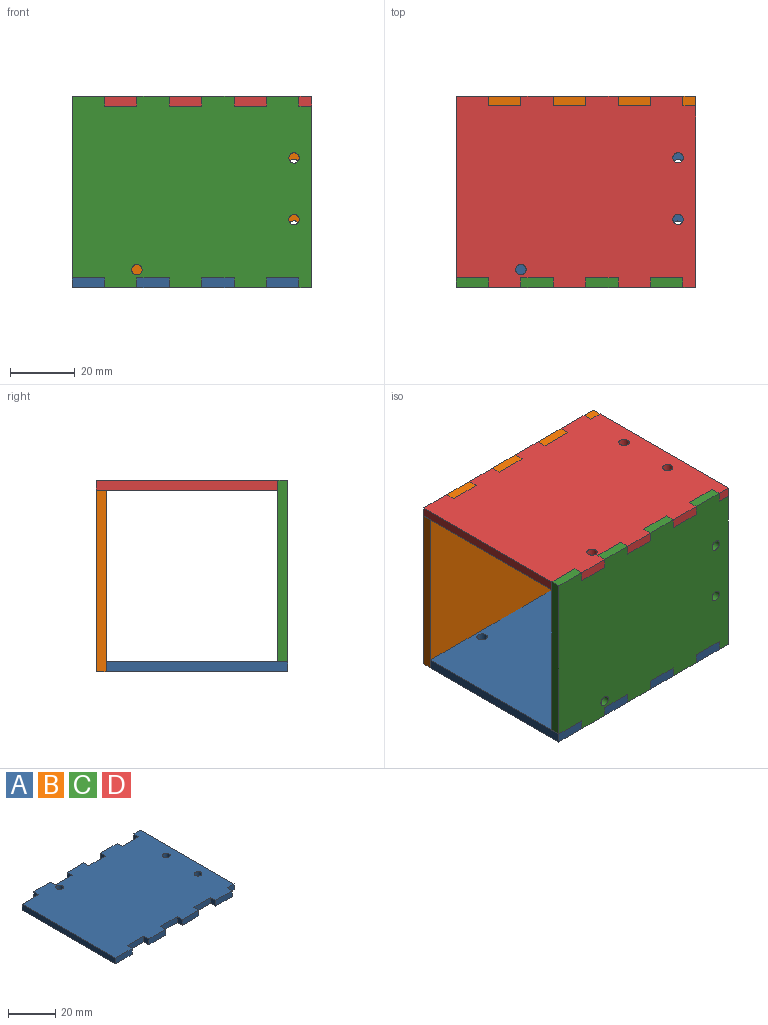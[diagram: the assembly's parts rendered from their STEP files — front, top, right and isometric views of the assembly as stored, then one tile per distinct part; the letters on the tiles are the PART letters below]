
ASSEMBLY  parts=4 mates=3
PART A: 37 faces, bbox 74x59x3 mm
  f0: plane 3x3mm, normal (1,0,0), area 9mm2, adj f1,f34,f35,f36
  f1: plane 4x3mm, normal (0,-1,0), area 12mm2, adj f0,f2,f35,f36
  f2: plane 56x3mm, normal (1,0,0), area 168mm2, adj f1,f3,f35,f36
  f3: plane 4x3mm, normal (0,1,0), area 12mm2, adj f2,f4,f35,f36
  f4: plane 3x3mm, normal (-1,0,0), area 9mm2, adj f3,f5,f35,f36
  f5: plane 10x3mm, normal (0,1,0), area 30mm2, adj f4,f6,f35,f36
  f6: plane 3x3mm, normal (1,0,0), area 9mm2, adj f5,f7,f35,f36
  f7: plane 10x3mm, normal (0,1,0), area 30mm2, adj f6,f8,f35,f36
  f8: plane 3x3mm, normal (-1,0,0), area 9mm2, adj f7,f9,f35,f36
  f9: plane 10x3mm, normal (0,1,0), area 30mm2, adj f8,f10,f35,f36
  f10: plane 3x3mm, normal (1,0,0), area 9mm2, adj f9,f11,f35,f36
  f11: plane 10x3mm, normal (0,1,0), area 30mm2, adj f10,f12,f35,f36
  f12: plane 3x3mm, normal (-1,0,0), area 9mm2, adj f11,f13,f35,f36
  f13: plane 10x3mm, normal (0,1,0), area 30mm2, adj f12,f14,f35,f36
  f14: plane 3x3mm, normal (1,0,0), area 9mm2, adj f13,f15,f35,f36
  f15: plane 10x3mm, normal (0,1,0), area 30mm2, adj f14,f16,f35,f36
  f16: plane 3x3mm, normal (-1,0,0), area 9mm2, adj f15,f17,f35,f36
  f17: plane 10x3mm, normal (0,1,0), area 30mm2, adj f16,f18,f35,f36
  f18: plane 56x3mm, normal (-1,0,0), area 168mm2, adj f17,f19,f35,f36
  f19: plane 10x3mm, normal (0,-1,0), area 30mm2, adj f18,f20,f35,f36
  f20: plane 3x3mm, normal (1,0,0), area 9mm2, adj f19,f21,f35,f36
  f21: plane 10x3mm, normal (0,-1,0), area 30mm2, adj f20,f22,f35,f36
  f22: plane 3x3mm, normal (-1,0,0), area 9mm2, adj f21,f23,f35,f36
  f23: plane 10x3mm, normal (0,-1,0), area 30mm2, adj f22,f24,f35,f36
  f24: plane 3x3mm, normal (1,0,0), area 9mm2, adj f23,f25,f35,f36
  f25: plane 10x3mm, normal (0,-1,0), area 30mm2, adj f24,f26,f35,f36
  f26: plane 3x3mm, normal (-1,0,0), area 9mm2, adj f25,f27,f35,f36
  f27: plane 10x3mm, normal (0,-1,0), area 30mm2, adj f26,f28,f35,f36
  f28: plane 3x3mm, normal (1,0,0), area 9mm2, adj f27,f29,f35,f36
  f29: plane 10x3mm, normal (0,-1,0), area 30mm2, adj f28,f30,f35,f36
  f30: plane 3x3mm, normal (-1,0,0), area 9mm2, adj f29,f34,f35,f36
  f31: cylinder r=1.6mm len=3.2mm, axis (0,0,-1), area 30.2mm2, adj f35,f36
  f32: cylinder r=1.6mm len=3.2mm, axis (0,0,-1), area 30.2mm2, adj f35,f36
  f33: cylinder r=1.6mm len=3.2mm, axis (0,0,-1), area 30.2mm2, adj f35,f36
  f34: plane 10x3mm, normal (0,-1,0), area 30mm2, adj f0,f30,f35,f36
  f35: plane 74x59mm, normal (0,0,1), area 4119.9mm2, adj f0,f1,f2,f3,f4,f5,f6,f7
  f36: plane 74x59mm, normal (0,0,-1), area 4119.9mm2, adj f0,f1,f2,f3,f4,f5,f6,f7
PART B: same geometry as A
PART C: same geometry as A
PART D: same geometry as A
PLACE A rot(axis=(-1,0,0),0deg) t=(46.9,-46.6,-120.83)mm
PLACE B rot(axis=(1,0,0),90deg) t=(46.9,-17.1,-91.33)mm
PLACE C rot(axis=(-1,0,0),90deg) t=(46.9,-76.1,-91.33)mm
PLACE D rot(axis=(1,0,0),180deg) t=(46.9,-46.6,-61.83)mm
MATE fastened A.f0 <-> C.f4  axis (1,0,0) through (79.9,-74.6,-119.33)mm
MATE fastened C.f0 <-> D.f4  axis (1,0,0) through (79.9,-74.6,-63.33)mm
MATE fastened B.f0 <-> A.f4  axis (1,0,0) through (79.9,-18.6,-119.33)mm
